# Revit family: Urinal_System-Top_Spud-American_Standard-Washbrook-6501_Series
name_source: partatom
category: Plumbing Fixtures
revit_build: Autodesk Revit 2018 (Build: 20170223_1515(x64)
units: mm (PartAtom-declared; Revit-internal decimal feet)

## family parameters
Cut with Voids When Loaded = No
Host = Face
OmniClass Number = 23.45.05.21.11.21
OmniClass Title = Urinals
Part Type = Normal
Room Calculation Point = No
Round Connector Dimension = Use Radius
Shared = Yes

## types (3) — shared parameters
ADA Compliant = Yes
Assembly Code = D2010210
Body Material = Ceramic-American_Standard-Vitreous_China-White
CW Connection = Yes
CWFU = 5
Cold Water Connection Diameter = 3/4"
Cold Water Connection Height = 11 1/2"
Cold Water Connection Radius = 3/8"
Cold Water Connection Width = 4 3/4"
Default Elevation = 17"
Flow Rate = 10gpm (37.9 L/min.)
Flush Rate = 0.125 gpf to 1.0 gpf (0.5 Lpf to 3.8 Lpf)
HW Connection = No
Height = 26 1/8"
Installation Type = Wall Mounted
Length = 18 7/8"
Manufacturer = American Standard
Price = Prices may vary. Please consult Manufacturer Representative for most up-to-date price list.
Product Documentation Link = https://www.americanstandard-us.com
Product Page URL = https://www.americanstandard-us.com
Revised Date = 01/29/2021
Shipping Weight = 56lbs (25.3kg)
URL = http://www.americanstandard-us.com
Vent Connection = No
WFU = 5
Warranty Information = 1 Year Limited Warranty
Waste Connection = Yes
Waste Connection Diameter = 2"
Waste Connection Height = 20 1/2"
Waste Connection Radius = 1"
Width = 14 1/8"
Working Pressure = 20 psi (flowing) - 80 psi (static)
zero-valued in all types: HWFU

## per-type parameters (varying)
| type | Description | Flushvalve |
| 6501.511.020 | 1.0 gpf Exposed Top Spud Urinal and Manual Piston-Type Urinal Flush Valve | Flush_Valve-Urinal-American_Standard-Exposed-Top_Spud-Manual_Series : 6045.101 |
| 6501.610.020 | 1.0 gpf Exposed Top Spud Urinal and Selectronic® Urinal Flush Valve | Flush_Valve-Urinal_Exposed-American_Standard-Selectronic_Series : 6063.101.002 |
| 6501.615.020 | 1.0 gpf Exposed Top Spud Urinal and Selectronic® Exposed AC Urinal Flush Valve | Flush_Valve-Urinal_Exposed-American_Standard-Selectronic-6062.101 : 6062.101.002 |

note: column(s) folded — value = type name in every type: Model

## geometry (parser evidence)
native form markers: Sweep x8
no freeform markers — native parametric forms only
